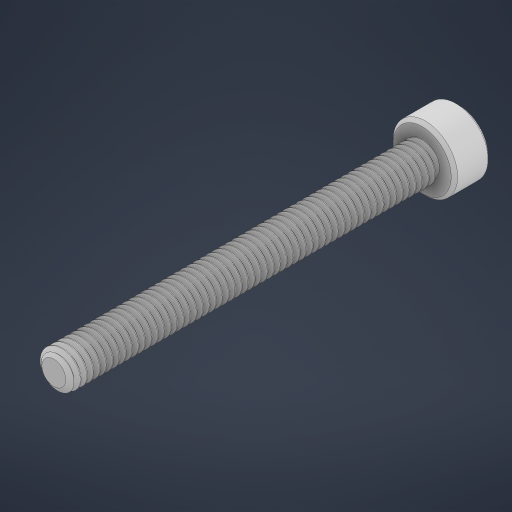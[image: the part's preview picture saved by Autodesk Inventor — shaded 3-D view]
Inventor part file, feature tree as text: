
AUTODESK INVENTOR PART (.ipt)
format: ipt  version: 2023 (Build 270158000, 158)  size: 1,561,088 bytes
history: native  units: in
note: dims shown in document units (in); Inventor stores cm internally (conversion verified against a paired STEP export)
features: chamfer x1
ambient origin geometry x8: Origin, YZ Plane, XZ Plane, XY Plane, X Axis, Y Axis, Z Axis, Center Point
bodies: Solid1 (feature_tree)
feature tree (1):
  chamfer  "Chamfer1"  [1 undecoded]
note: 1 required parameter value undecoded (feature->parameter linkage not recoverable at this tier; creation-order binding heuristic only, values carry confidence <= 0.55)
